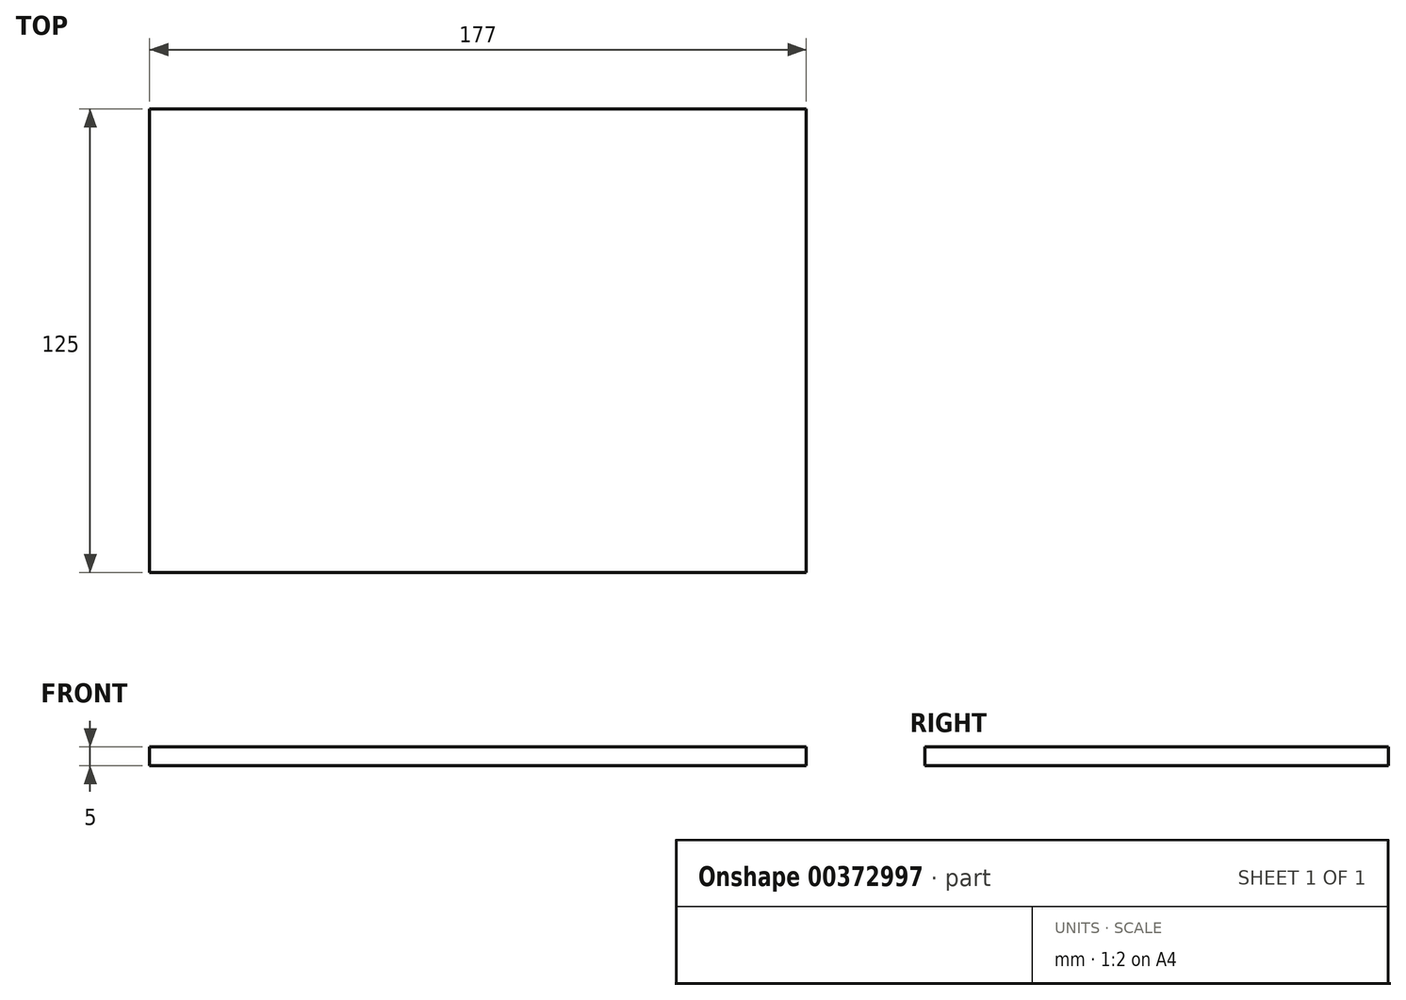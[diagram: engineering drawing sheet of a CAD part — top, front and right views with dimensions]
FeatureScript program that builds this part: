
annotation { "Feature Type Name" : "Feature", "Feature Type Description" : "" }
export const myFeature = defineFeature(function(context is Context, id is Id, definition is map)
    precondition{}
    {
        {
            var Q0;
            Q0=qCreatedBy(makeId("Top.planeOp"),FACE);
            var sketch = newSketch(context, id + "F0", { "sketchPlane" : qUnion([Q0])});
            skLineSegment(sketch, "E0.bottom", {"start": v(-88.5, 62.5) * mm, "end": v(88.5, 62.5) * mm});
            skLineSegment(sketch, "E0.top", {"start": v(-88.5, -62.5) * mm, "end": v(88.5, -62.5) * mm});
            skLineSegment(sketch, "E0.left", {"start": v(-88.5, 62.5) * mm, "end": v(-88.5, -62.5) * mm});
            skLineSegment(sketch, "E0.right", {"start": v(88.5, 62.5) * mm, "end": v(88.5, -62.5) * mm});
            skPoint(sketch, "E0.middle", {"position": v(0, 0) * mm});
            skSolve(sketch);
        }
        {
            var Q0;
            Q0 = qSketchRegion(id + "F0", true);
            extrude(context, id + "F1", {"entities" : qUnion([Q0]), "depth" : 5 * mm});
        }
    });
